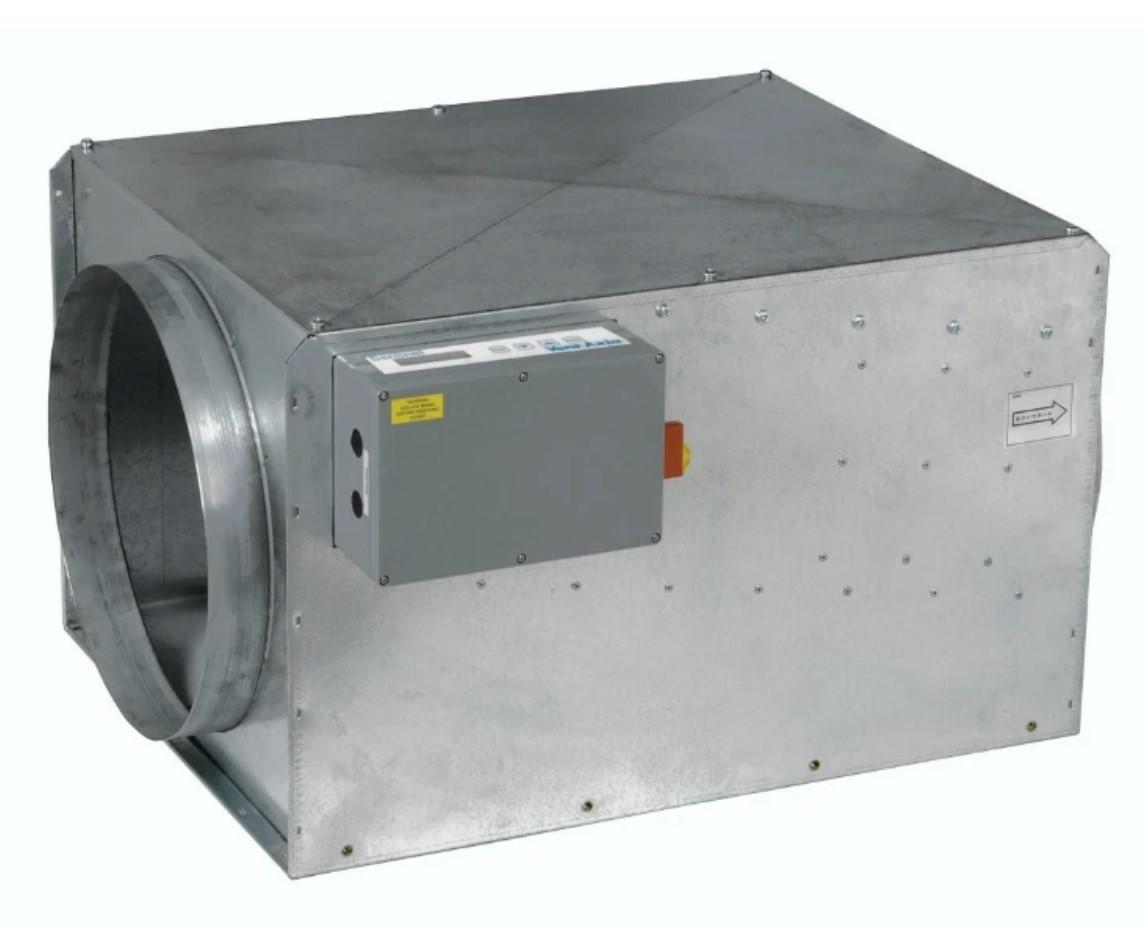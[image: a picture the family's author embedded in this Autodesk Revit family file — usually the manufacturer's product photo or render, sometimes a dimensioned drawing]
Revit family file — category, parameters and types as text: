
# Revit family: CADS_Vent-Axia_MechEquip_Fan_SENT_DBoxSingle - SUPPLY
name_source: partatom
category: Mechanical Equipment
units: mm (PartAtom-declared; Revit-internal decimal feet)

## family parameters
Classification = None
Cut with Voids When Loaded = No
Host = Face
OmniClass Number = 23.75.35.17.11
OmniClass Title = Fans for Air Ductwork
Part Type = Normal
Room Calculation Point = No
Round Connector Dimension = Use Diameter
Shared = No

## types (11) — shared parameters
AirflowRateRange = 0.0 L/s
AssemblyPlace = UNKNOWN
AssetType = FIXED
Default Elevation = 1219 mm
DurationUnit = Year
ExteriorInsulation = No
Fitting Type = Ignore
GrossWeight = 0.00 kg
HasProtectiveEarth = No
IsExtendedWarranty = No
ManufacturerAddress = Fleming Way
Crawley 
RH10 9YX
Quantity = 1
RatedCurrent = 0 A
RatedVoltage = 0 V
Status = New
WarrantyGuarantor = Vent-Axia Limited
WorkingPressure = 0.0 Pa
zero-valued in all types: CADS_Index, CADS_Usage, ExpectedServiceLife, H, NumberOfPoles, W

## per-type parameters (varying)
| type | EBHoffset | EBVoffset | L | ModelReference | NominalDiameter | NominalHeight | NominalLength | NominalWidth | OutOffset | SpigotCLHeight | Type Image |
| SENT100S | 75 mm | 70 mm | 360 mm | SENTINEL 100S/H | 100 mm  [stored 0.328084 ft] | 192 mm  [stored 0.629921 ft] | 380 mm | 306 mm  [stored 1.00394 ft] | 62 mm  [stored 0.203412 ft] | 62 mm  [stored 0.203412 ft] | <None> |
| SENT125S | 206 mm | 80 mm | 360 mm | SENTINEL 125 HIERARCHY | 125 mm  [stored 0.410105 ft] | 192 mm  [stored 0.629921 ft] | 380 mm | 306 mm  [stored 1.00394 ft] | 62 mm  [stored 0.203412 ft] | 62 mm  [stored 0.203412 ft] | <None> |
| SENT150S | 206 mm | 80 mm | 360 mm | SENTINEL 150 HIERARCHY | 150 mm | 192 mm  [stored 0.629921 ft] | 380 mm | 306 mm  [stored 1.00394 ft] | 62 mm  [stored 0.203412 ft] | 62 mm  [stored 0.203412 ft] | <None> |
| SENT150S/CP | 206 mm | 80 mm | 360 mm | SENTINEL 150 CONST.PRESS | 150 mm | 192 mm  [stored 0.629921 ft] | 380 mm | 306 mm  [stored 1.00394 ft] | 62 mm  [stored 0.203412 ft] | 62 mm  [stored 0.203412 ft] | <None> |
| SENT200S | 206 mm | 80 mm | 415 mm | SENTINEL 200 HIERARCHY | 200 mm  [stored 0.656168 ft] | 287 mm | 435 mm | 360 mm | 60 mm | 60 mm | <None> |
| SENT250S | 206 mm | 80 mm | 415 mm | SENTINEL 250 HIERARCHY | 250 mm  [stored 0.82021 ft] | 287 mm | 435 mm | 360 mm | 35 mm | 35 mm | <None> |
| SENT315S | 206 mm | 80 mm | 690 mm | SENTINEL 315 HIERARCHY | 315 mm | 458 mm | 710 mm | 568 mm | 43 mm | 43 mm | <None> |
| SENT315S/CP | 206 mm | 80 mm | 690 mm | SENTINEL 315 CONST.PRESS | 315 mm | 458 mm | 710 mm | 568 mm | 43 mm | 43 mm | <None> |
| SENT400S | 206 mm | 80 mm | 690 mm | SENTINEL 400 HIERARCHY | 400 mm | 458 mm | 710 mm | 568 mm | 43 mm | 43 mm | <None> |
| SENT400S/CP | 206 mm | 80 mm | 690 mm | SENTINEL 400 CONST.PRESS | 400 mm | 458 mm | 710 mm | 568 mm | 43 mm | 43 mm | <None> |
| SENT500S | 206 mm | 80 mm | 878 mm | SENTINEL 500 HIERARCHY | 500 mm | 577 mm | 898 mm | 765 mm | 59 mm | 59 mm | CADS_Vent-Axia_MechEquip_Fan_SENT_DBoxSingle.jpg |

note: column(s) folded — value = type name in every type: ModelNumber

note: [stored X ft] marks values corroborated as IEEE doubles in the binary element streams (Revit-internal decimal feet)

## geometry (parser evidence)
native form markers: Sweep x3
no freeform markers — native parametric forms only
